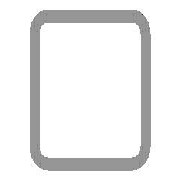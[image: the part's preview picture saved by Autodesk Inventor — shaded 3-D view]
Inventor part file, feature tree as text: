
AUTODESK INVENTOR PART (.ipt)
format: ipt  version: 2025 (Build 290162010, 162A)  size: 165,376 bytes
history: native  units: mm (DEFAULTED — no unit token found)
features: other x3, sketch x3, projected_geometry x2, extrude x1, plane x1
ambient origin geometry x8: Origin, YZ Plane, XZ Plane, XY Plane, X Axis, Y Axis, Z Axis, Center Point
bodies: Solid1 (feature_tree), Body (feature_tree)
feature tree (10):
  other  "Driven Length"
  other  "Start plane"
  other  "End plane"
  sketch  "Sketch5"  dims[d7=8.0mm]
  extrude  "Extrusion2"  TaperAngle=0.0deg  [1 undecoded]
  sketch  "Sketch3"  dims[d3=1000.0mm d4=0.0mm]
  plane  "Work Plane3"
  sketch  "Sketch6"  dims[d9=150.0mm d11=150.0mm d12=4.0mm d13=-0.0mm d14=1000.0mm d15=75.0mm d16=75.0mm d17=90.0deg d18=1000.0mm d22=1100.0mm d24=3000.0mm d25=285.0mm d26=40.0mm d27=3000.0mm d28=600.0mm d30=808.942853mm d31=0.0mm d32=0.0mm d33=10.0mm]
  projected_geometry  "Projected Loop1"
  projected_geometry  "Projected Loop2"
note: 1 required parameter value undecoded (feature->parameter linkage not recoverable at this tier; creation-order binding heuristic only, values carry confidence <= 0.55)
